# Revit family: ef_eg-20_40ysxc2_a(t)sxc2_b(t)sxc2_d(t)sxc2_csxc2-q_50Hz
name_source: partatom
category: 機械設備
units: mm (PartAtom-declared; Revit-internal decimal feet)

## family parameters
OmniClass タイトル = Industrial Ventilating Equipment
OmniClass 番号 = 23.75.35.21.17
パーツ タイプ = 標準
ロード時にボイドで切り取り = はい
丸型コネクタ寸法 = 直径を使用
作業面ベース = いいえ
共有 = いいえ
常に垂直 = はい
部屋計算ポイント = はい

## types (11) — shared parameters
IfcExportAs = IfcFanType
IfcExportType = TUBEAXIAL
MID風量 = 0.0 m³/h
MIN風量 = 0.0 m³/h
OmniClassCode = 23-33 31 19 11 17
URL = https://www.mitsubishielectric.co.jp
Uniclass2015Code = Pr_65_67_29_67
Uniclass2015Title = Propeller fans
Uniclass2015Version = Systems v1.9
オリフィス_Depth = 45
ファンの種類 = 軸流羽根
レグ_Height = 413
レグ_Width = 413
仕様書バージョン = Version1.0
企業コード = 108420
分類コード = 50052503100110
周波数 = 50 Hz
呼称 = 有圧扇
法定耐用年数 = 15
製品リリース年月 = 2022年6月1日
製品出荷対象 = 国内
製造元 = 三菱電機株式会社
設置方法 = 壁付
説明 = 産業用有圧換気扇 低騒音形ステンレスタイプ オールステンレスタイプ 給気専用
負荷分類 = 3_ファン類
運転質量 = 0.00 kg

## per-type parameters (varying)
| type | Box_H | Box_W | Depth | Height | MAX風量 | Width | オリフィス径 | フレームの厚さ | ボックス_Depth | ボックス_Height | ボックス_Width | モデル | モーター径 | レグ_Depth | 価格 | 極 | 極数 | 消費電力 | 相 | 羽根径 | 製品質量 | 質量 | 電動機出力 | 電圧 |
| EF-20YSXC2-Q | 84 | 117 | 224  [stored 0.734908 ft] | 320  [stored 1.04987 ft] | 660.0 m³/h | 320  [stored 1.04987 ft] | 257  [stored 0.843176 ft] | 71  [stored 0.23294 ft] | 101 | 103 | 38 | EF-20YSXC2-Q | 99  [stored 0.324803 ft] | 208 | 156000 $ | 4 | 2 | 27 W | 1 | ∅200 | 5.30 kg | 6.36 kg | 15 W | 100 V |
| EF-25ASXC2-Q | 83 | 137 | 224  [stored 0.734908 ft] | 370 | 1080.0 m³/h | 370 | 298 | 71  [stored 0.23294 ft] | 106 | 131  [stored 0.42979 ft] | 46 | EF-25ASXC2-Q | 99  [stored 0.324803 ft] | 208 | 161000 $ | 4 | 2 | 53 W | 1 | ∅250 | 6.00 kg | 7.20 kg | 25 W | 100 V |
| EF-30BSXC2-Q | 108 | 162 | 224  [stored 0.734908 ft] | 420 | 1680.0 m³/h | 420 | 348 | 71  [stored 0.23294 ft] | 106 | 131  [stored 0.42979 ft] | 46 | EF-30BSXC2-Q | 99  [stored 0.324803 ft] | 208 | 216000 $ | 4 | 2 | 63 W | 1 | ∅300 | 7.00 kg | 8.40 kg | 50 W | 100 V |
| EF-40DSXC2-Q | 185 | 213 | 286 | 520 | 3760.0 m³/h | 520 | 476 | 71  [stored 0.23294 ft] | 119 | 131  [stored 0.42979 ft] | 47 | EF-40DSXC2-Q | 113 | 250  [stored 0.82021 ft] | 270000 $ | 4 | 2 | 130 W | 1 | ∅400 | 15.00 kg | 18.00 kg | 200 W | 100 V |
| EG-40CSXC2-Q | 185 | 213 | 321 | 520 | 3060.0 m³/h | 520 | 476 | 106 | 154 | 131  [stored 0.42979 ft] | 47 | EG-40CSXC2-Q | 113 | 285 | 258000 $ | 6 | 2 | 100 W | 1 | ∅400 | 15.50 kg | 18.60 kg | 100 W | 100 V |
| EF-25ATXC2-Q_200V | 83 | 137 | 224  [stored 0.734908 ft] | 370 | 1080.0 m³/h | 370 | 298 | 71  [stored 0.23294 ft] | 106 | 131  [stored 0.42979 ft] | 46 | EF-25ATXC2-Q | 99  [stored 0.324803 ft] | 208 | 161000 $ | 4 | 3 | 35 W | 3 | ∅250 | 6.50 kg | 7.80 kg | 25 W | 200 V |
| EF-30BTXC2-Q_200V | 108 | 162 | 224  [stored 0.734908 ft] | 420 | 1680.0 m³/h | 420 | 348 | 71  [stored 0.23294 ft] | 106 | 131  [stored 0.42979 ft] | 46 | EF-30BTXC2-Q | 99  [stored 0.324803 ft] | 208 | 216000 $ | 4 | 3 | 56 W | 3 | ∅300 | 7.50 kg | 9.00 kg | 50 W | 200 V |
| EF-40DTXC2-Q_200V | 185 | 213 | 286 | 520 | 3760.0 m³/h | 520 | 476 | 71  [stored 0.23294 ft] | 119 | 131  [stored 0.42979 ft] | 47 | EF-40DTXC2-Q | 113 | 250  [stored 0.82021 ft] | 270000 $ | 4 | 3 | 124 W | 3 | ∅400 | 15.00 kg | 18.00 kg | 200 W | 200 V |
| EF-25ATXC2-Q_220V | 83 | 137 | 224  [stored 0.734908 ft] | 370 | 1080.0 m³/h | 370 | 298 | 71  [stored 0.23294 ft] | 106 | 131  [stored 0.42979 ft] | 46 | EF-25ATXC2-Q | 99  [stored 0.324803 ft] | 208 | 161000 $ | 4 | 3 | 42 W | 3 | ∅250 | 6.50 kg | 7.80 kg | 25 W | 220 V |
| EF-30BTXC2-Q_220V | 108 | 162 | 224  [stored 0.734908 ft] | 420 | 1680.0 m³/h | 420 | 348 | 71  [stored 0.23294 ft] | 106 | 131  [stored 0.42979 ft] | 46 | EF-30BTXC2-Q | 99  [stored 0.324803 ft] | 208 | 216000 $ | 4 | 3 | 72 W | 3 | ∅300 | 7.50 kg | 9.00 kg | 50 W | 220 V |
| EF-40DTXC2-Q_220V | 185 | 213 | 286 | 520 | 3760.0 m³/h | 520 | 476 | 71  [stored 0.23294 ft] | 119 | 131  [stored 0.42979 ft] | 47 | EF-40DTXC2-Q | 113 | 250  [stored 0.82021 ft] | 270000 $ | 4 | 3 | 135 W | 3 | ∅400 | 15.00 kg | 18.00 kg | 200 W | 220 V |

note: [stored X ft] marks values corroborated as IEEE doubles in the binary element streams (Revit-internal decimal feet)
